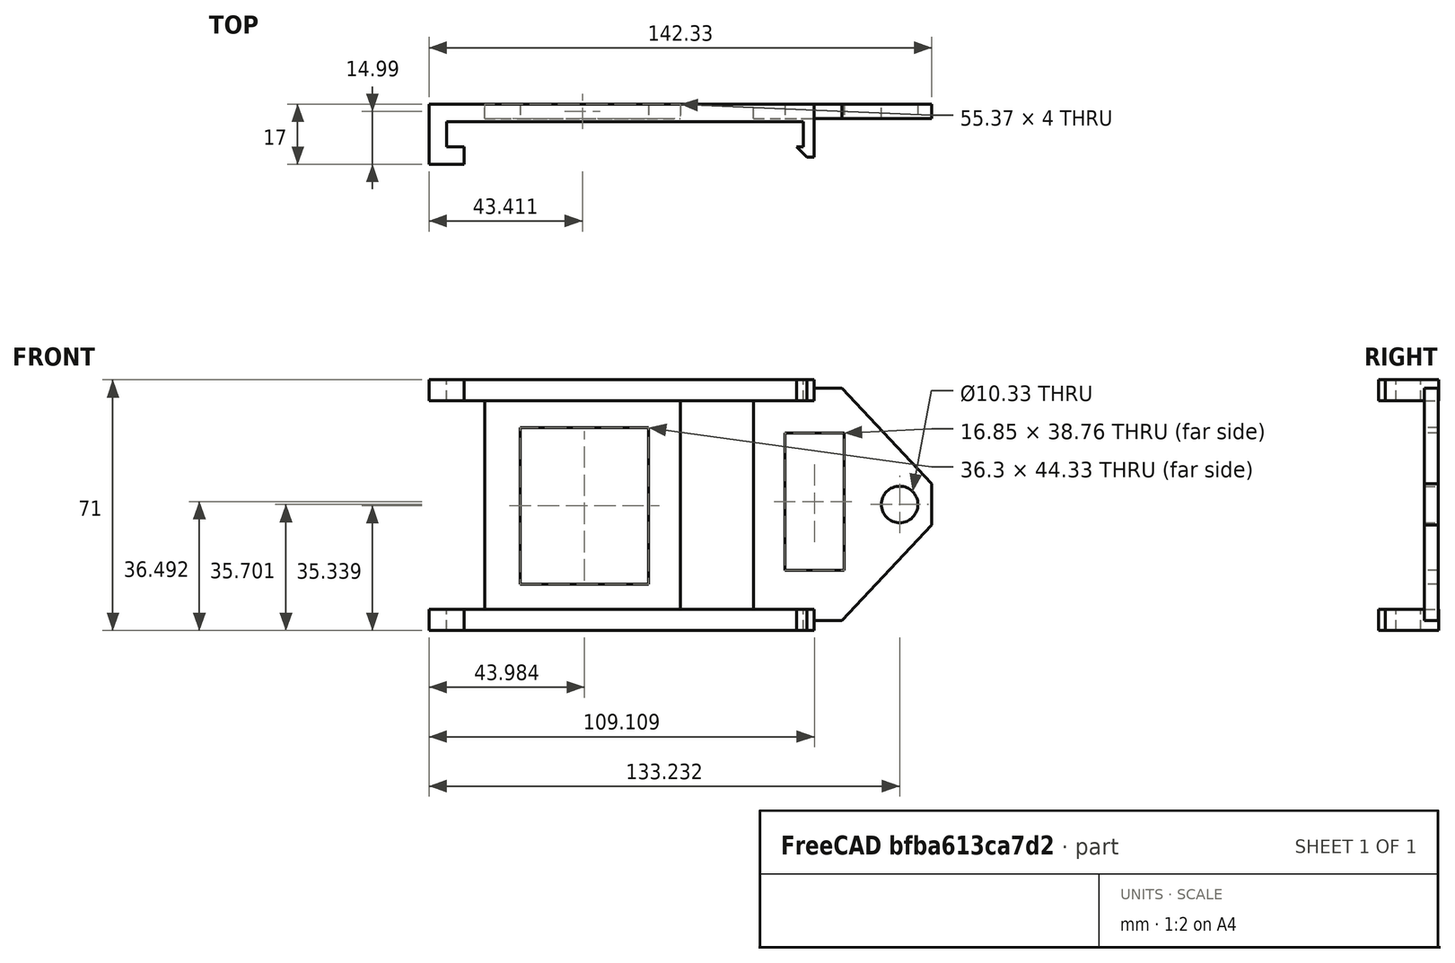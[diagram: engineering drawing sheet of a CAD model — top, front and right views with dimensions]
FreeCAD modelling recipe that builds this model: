
FCSTD DOCUMENT  (FreeCAD 0.19R24415 (Git))
Label: halter_wohnwagen
License: All rights reserved
LicenseURL: http://en.wikipedia.org/wiki/All_rights_reserved
objects: Sketcher::SketchObject×7, PartDesign::Pad×7, PartDesign::Body×7, Part::Cut×3, Part::Fuse×3, Mesh::Feature×1
note: 34 computed .brp shape members not serialized (recipe doc carries the construction recipe); baked Part::Feature solids carry a one-line shape summary decoded from their .brp

FEATURE [Sketcher::SketchObject] Sketch
  FullyConstrained = false
  MapMode = 5
  Support = -> [XY_Plane]
  sketch-geometry (12):
    g0: LineSegment StartX=87.2327 StartY=56.8132 StartZ=0 EndX=188.233 EndY=56.8132 EndZ=0
    g1: LineSegment StartX=188.233 StartY=56.8132 StartZ=0 EndX=188.233 EndY=49.8132 EndZ=0
    g2: LineSegment StartX=188.233 StartY=49.8132 StartZ=0 EndX=186.233 EndY=49.8132 EndZ=0
    g3: LineSegment StartX=186.233 StartY=49.8132 StartZ=0 EndX=189.233 EndY=46.8132 EndZ=0
    g4: LineSegment StartX=189.233 StartY=46.8132 StartZ=0 EndX=191.233 EndY=46.8132 EndZ=0
    g5: LineSegment StartX=191.233 StartY=46.8132 StartZ=0 EndX=191.233 EndY=61.8132 EndZ=0
    g6: LineSegment StartX=191.233 StartY=61.8132 StartZ=0 EndX=82.2327 EndY=61.8132 EndZ=0
    g7: LineSegment StartX=82.2327 StartY=61.8132 StartZ=0 EndX=82.2327 EndY=44.8132 EndZ=0
    g8: LineSegment StartX=82.2327 StartY=44.8132 StartZ=0 EndX=92.2327 EndY=44.8132 EndZ=0
    g9: LineSegment StartX=92.2327 StartY=44.8132 StartZ=0 EndX=92.2327 EndY=49.8132 EndZ=0
    g10: LineSegment StartX=92.2327 StartY=49.8132 StartZ=0 EndX=87.2327 EndY=49.8132 EndZ=0
    g11: LineSegment StartX=87.2327 StartY=49.8132 StartZ=0 EndX=87.2327 EndY=56.8132 EndZ=0
  constraints (34):
    c: Horizontal(g0)
    c: Coincident(g0,g1)
    c: Vertical(g1)
    c: Coincident(g1,g2)
    c: Coincident(g2,g3)
    c: Coincident(g3,g4)
    c: Coincident(g4,g5)
    c: Vertical(g5)
    c: Coincident(g5,g6)
    c: Horizontal(g6)
    c: Coincident(g6,g7)
    c: Vertical(g7)
    c: Coincident(g7,g8)
    c: Horizontal(g8)
    c: Coincident(g8,g9)
    c: Vertical(g9)
    c: Coincident(g9,g10)
    c: Horizontal(g10)
    c: Coincident(g10,g11)
    c: Coincident(g11,g0)
    c: Vertical(g11)
    c: DistanceY(g9,g9) = 5
    c: DistanceX(g6,g0) = 5
    c: DistanceY(g0,g6) = 5
    c: DistanceX(g0,g5) = 3
    c: Horizontal(g2)
    c: Horizontal(g4)
    c: DistanceX(g0,g0) = 101
    c: DistanceY(g11,g11) = 7
    c: DistanceY(g1,g1) = 7
    c: DistanceY(g4,g1) = 3
    c: DistanceX(g2,g1) = 2
    c: DistanceX(g4,g4) = 2
    c: DistanceX(g10,g10) = 5
FEATURE [PartDesign::Pad] Pad
  Direction = (1,1,1)
  Length = 6
  Length2 = 100
  Profile = -> Sketch
  Refine = true
  Type = 0
FEATURE [PartDesign::Body] Body  label="Halter1"
  Group = -> [Sketch,Pad]
  Origin = -> Origin
  Tip = -> Pad
FEATURE [Sketcher::SketchObject] Sketch001
  FullyConstrained = false
  MapMode = 5
  Support = -> [XY_Plane001]
  sketch-geometry (12):
    g0: LineSegment StartX=87.2327 StartY=56.8132 StartZ=0 EndX=188.233 EndY=56.8132 EndZ=0
    g1: LineSegment StartX=188.233 StartY=56.8132 StartZ=0 EndX=188.233 EndY=49.8132 EndZ=0
    g2: LineSegment StartX=188.233 StartY=49.8132 StartZ=0 EndX=186.233 EndY=49.8132 EndZ=0
    g3: LineSegment StartX=186.233 StartY=49.8132 StartZ=0 EndX=189.233 EndY=46.8132 EndZ=0
    g4: LineSegment StartX=189.233 StartY=46.8132 StartZ=0 EndX=191.233 EndY=46.8132 EndZ=0
    g5: LineSegment StartX=191.233 StartY=46.8132 StartZ=0 EndX=191.233 EndY=61.8132 EndZ=0
    g6: LineSegment StartX=191.233 StartY=61.8132 StartZ=0 EndX=82.2327 EndY=61.8132 EndZ=0
    g7: LineSegment StartX=82.2327 StartY=61.8132 StartZ=0 EndX=82.2327 EndY=44.8132 EndZ=0
    g8: LineSegment StartX=82.2327 StartY=44.8132 StartZ=0 EndX=92.2327 EndY=44.8132 EndZ=0
    g9: LineSegment StartX=92.2327 StartY=44.8132 StartZ=0 EndX=92.2327 EndY=49.8132 EndZ=0
    g10: LineSegment StartX=92.2327 StartY=49.8132 StartZ=0 EndX=87.2327 EndY=49.8132 EndZ=0
    g11: LineSegment StartX=87.2327 StartY=49.8132 StartZ=0 EndX=87.2327 EndY=56.8132 EndZ=0
  constraints (34):
    c: Horizontal(g0)
    c: Coincident(g0,g1)
    c: Vertical(g1)
    c: Coincident(g1,g2)
    c: Coincident(g2,g3)
    c: Coincident(g3,g4)
    c: Coincident(g4,g5)
    c: Vertical(g5)
    c: Coincident(g5,g6)
    c: Horizontal(g6)
    c: Coincident(g6,g7)
    c: Vertical(g7)
    c: Coincident(g7,g8)
    c: Horizontal(g8)
    c: Coincident(g8,g9)
    c: Vertical(g9)
    c: Coincident(g9,g10)
    c: Horizontal(g10)
    c: Coincident(g10,g11)
    c: Coincident(g11,g0)
    c: Vertical(g11)
    c: DistanceY(g9,g9) = 5
    c: DistanceX(g6,g0) = 5
    c: DistanceY(g0,g6) = 5
    c: DistanceX(g0,g5) = 3
    c: Horizontal(g2)
    c: Horizontal(g4)
    c: DistanceX(g0,g0) = 101
    c: DistanceY(g11,g11) = 7
    c: DistanceY(g1,g1) = 7
    c: DistanceY(g4,g1) = 3
    c: DistanceX(g2,g1) = 2
    c: DistanceX(g4,g4) = 2
    c: DistanceX(g10,g10) = 5
FEATURE [PartDesign::Pad] Pad001
  Direction = (1,1,1)
  Length = 6
  Length2 = 100
  Profile = -> Sketch001
  Refine = true
  Type = 0
FEATURE [PartDesign::Body] Body001  label="Halter2"
  Group = -> [Sketch001,Pad001]
  Origin = -> Origin001
  Placement = pos=(0,0,-65) rot=(0,0,1;0rad)
  Tip = -> Pad001
FEATURE [Sketcher::SketchObject] Sketch002
  FullyConstrained = false
  MapMode = 5
  Placement = pos=(0,0,0) rot=(1,0,0;1.5708rad)
  Support = -> [XZ_Plane002]
  sketch-geometry (6):
    g0: LineSegment StartX=174.138 StartY=3.58044 StartZ=0 EndX=199.138 EndY=3.58044 EndZ=0
    g1: LineSegment StartX=199.138 StartY=3.58044 StartZ=0 EndX=224.564 EndY=-23.449 EndZ=0
    g2: LineSegment StartX=224.564 StartY=-23.449 StartZ=0 EndX=224.564 EndY=-35.1539 EndZ=0
    g3: LineSegment StartX=224.564 StartY=-35.1539 StartZ=0 EndX=199.138 EndY=-62.1833 EndZ=0
    g4: LineSegment StartX=199.138 StartY=-62.1833 StartZ=0 EndX=174.138 EndY=-62.1833 EndZ=0
    g5: LineSegment StartX=174.138 StartY=-62.1833 StartZ=0 EndX=174.138 EndY=3.58044 EndZ=0
  constraints (13):
    c: Horizontal(g0)
    c: Coincident(g0,g1)
    c: Coincident(g1,g2)
    c: Coincident(g2,g3)
    c: Coincident(g3,g4)
    c: Coincident(g4,g5)
    c: Coincident(g5,g0)
    c: Vertical(g5)
    c: Equal(g0,g4)
    c: Equal(g1,g3)
    c: Horizontal(g4)
    c: DistanceX(g0,g0) = 25
    c: Vertical(g2)
FEATURE [PartDesign::Pad] Pad002
  Direction = (1,1,1)
  Length = 4
  Length2 = 100
  Placement = pos=(0,0,0) rot=(1,0,0;1.5708rad)
  Profile = -> Sketch002
  Refine = true
  Type = 0
FEATURE [PartDesign::Body] Body002
  Group = -> [Sketch002,Pad002]
  Origin = -> Origin002
  Placement = pos=(0,61.81,0) rot=(0,0,1;0rad)
  Tip = -> Pad002
FEATURE [Sketcher::SketchObject] Sketch003
  FullyConstrained = false
  MapMode = 5
  Placement = pos=(0,0,0) rot=(1,0,0;1.5708rad)
  Support = -> [XZ_Plane003]
  sketch-geometry (4):
    g0: LineSegment StartX=182.916 StartY=-9.12813 StartZ=0 EndX=199.762 EndY=-9.12813 EndZ=0
    g1: LineSegment StartX=199.762 StartY=-9.12813 StartZ=0 EndX=199.762 EndY=-47.887 EndZ=0
    g2: LineSegment StartX=199.762 StartY=-47.887 StartZ=0 EndX=182.916 EndY=-47.887 EndZ=0
    g3: LineSegment StartX=182.916 StartY=-47.887 StartZ=0 EndX=182.916 EndY=-9.12813 EndZ=0
  constraints (8):
    c: Coincident(g0,g1)
    c: Coincident(g1,g2)
    c: Coincident(g2,g3)
    c: Coincident(g3,g0)
    c: Horizontal(g0)
    c: Horizontal(g2)
    c: Vertical(g1)
    c: Vertical(g3)
FEATURE [PartDesign::Pad] Pad003
  Direction = (1,1,1)
  Length = 30
  Length2 = 100
  Placement = pos=(0,0,0) rot=(1,0,0;1.5708rad)
  Profile = -> Sketch003
  Refine = true
  Type = 0
FEATURE [PartDesign::Body] Body003
  Group = -> [Sketch003,Pad003]
  Origin = -> Origin003
  Placement = pos=(0,78,0) rot=(0,0,1;0rad)
  Tip = -> Pad003
FEATURE [Part::Cut] Cut
  Base = -> Body002
  Refine = true
  Tool = -> Body003
FEATURE [Sketcher::SketchObject] Sketch004
  FullyConstrained = false
  MapMode = 5
  Placement = pos=(0,0,0) rot=(1,0,0;1.5708rad)
  Support = -> [XZ_Plane004]
  sketch-geometry (1):
    g0: Circle CenterX=215.462 CenterY=-29.2989 CenterZ=0 NormalX=0 NormalY=0 NormalZ=1 AngleXU=0 Radius=5.16405
FEATURE [PartDesign::Pad] Pad004
  Direction = (1,1,1)
  Length = 100
  Length2 = 100
  Placement = pos=(0,0,0) rot=(1,0,0;1.5708rad)
  Profile = -> Sketch004
  Refine = true
  Type = 0
FEATURE [PartDesign::Body] Body004
  Group = -> [Sketch004,Pad004]
  Origin = -> Origin004
  Placement = pos=(0,110,0) rot=(0,0,1;0rad)
  Tip = -> Pad004
FEATURE [Part::Cut] Cut001
  Base = -> Cut
  Refine = true
  Tool = -> Body004
FEATURE [Sketcher::SketchObject] Sketch005
  FullyConstrained = false
  MapMode = 5
  Placement = pos=(0,0,0) rot=(1,0,0;1.5708rad)
  Support = -> [XZ_Plane005]
  sketch-geometry (4):
    g0: LineSegment StartX=97.9565 StartY=2.77657 StartZ=0 EndX=153.326 EndY=2.77657 EndZ=0
    g1: LineSegment StartX=153.326 StartY=2.77657 StartZ=0 EndX=153.326 EndY=-62.2953 EndZ=0
    g2: LineSegment StartX=153.326 StartY=-62.2953 StartZ=0 EndX=97.9565 EndY=-62.2953 EndZ=0
    g3: LineSegment StartX=97.9565 StartY=-62.2953 StartZ=0 EndX=97.9565 EndY=2.77657 EndZ=0
  constraints (8):
    c: Coincident(g0,g1)
    c: Coincident(g1,g2)
    c: Coincident(g2,g3)
    c: Coincident(g3,g0)
    c: Horizontal(g0)
    c: Horizontal(g2)
    c: Vertical(g1)
    c: Vertical(g3)
FEATURE [PartDesign::Pad] Pad005
  Direction = (1,1,1)
  Length = 4
  Length2 = 100
  Placement = pos=(0,0,0) rot=(1,0,0;1.5708rad)
  Profile = -> Sketch005
  Refine = true
  Type = 0
FEATURE [PartDesign::Body] Body005
  Group = -> [Sketch005,Pad005]
  Origin = -> Origin005
  Placement = pos=(0,61.8,0) rot=(0,0,1;0rad)
  Tip = -> Pad005
FEATURE [Sketcher::SketchObject] Sketch006
  FullyConstrained = false
  MapMode = 5
  Placement = pos=(0,0,0) rot=(1,0,0;1.5708rad)
  Support = -> [XZ_Plane006]
  sketch-geometry (4):
    g0: LineSegment StartX=108.064 StartY=-7.49618 StartZ=0 EndX=144.364 EndY=-7.49618 EndZ=0
    g1: LineSegment StartX=144.364 StartY=-7.49618 StartZ=0 EndX=144.364 EndY=-51.8254 EndZ=0
    g2: LineSegment StartX=144.364 StartY=-51.8254 StartZ=0 EndX=108.064 EndY=-51.8254 EndZ=0
    g3: LineSegment StartX=108.064 StartY=-51.8254 StartZ=0 EndX=108.064 EndY=-7.49618 EndZ=0
  constraints (8):
    c: Coincident(g0,g1)
    c: Coincident(g1,g2)
    c: Coincident(g2,g3)
    c: Coincident(g3,g0)
    c: Horizontal(g0)
    c: Horizontal(g2)
    c: Vertical(g1)
    c: Vertical(g3)
FEATURE [PartDesign::Pad] Pad006
  Direction = (1,1,1)
  Length = 100
  Length2 = 100
  Placement = pos=(0,0,0) rot=(1,0,0;1.5708rad)
  Profile = -> Sketch006
  Refine = true
  Type = 0
FEATURE [PartDesign::Body] Body006
  Group = -> [Sketch006,Pad006]
  Origin = -> Origin006
  Placement = pos=(0,110,0) rot=(0,0,1;0rad)
  Tip = -> Pad006
FEATURE [Part::Cut] Cut002
  Base = -> Body005
  Refine = true
  Tool = -> Body006
FEATURE [Part::Fuse] Fusion
  Base = -> Body
  Refine = true
  Tool = -> Body001
FEATURE [Part::Fuse] Fusion001
  Base = -> Cut002
  Refine = true
  Tool = -> Fusion
FEATURE [Part::Fuse] Fusion002
  Base = -> Cut001
  Refine = true
  Tool = -> Fusion001
FEATURE [Mesh::Feature] Mesh  label="Fusion002 (Meshed)"
